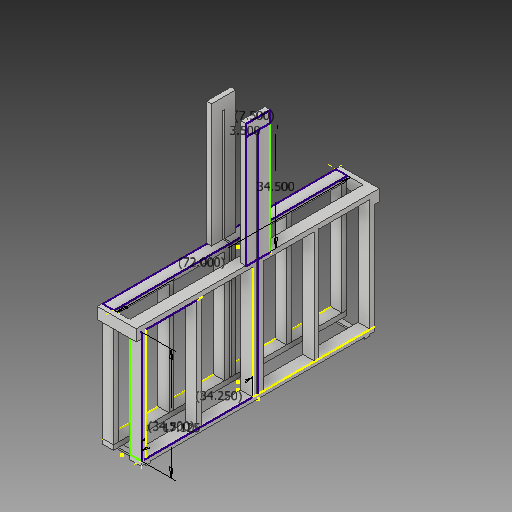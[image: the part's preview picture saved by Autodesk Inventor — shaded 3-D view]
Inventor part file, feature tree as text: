
AUTODESK INVENTOR PART (.ipt)
format: ipt  version: 2019 (Build 230136000, 136)  size: 366,080 bytes
history: native  units: in
note: dims shown in document units (in); Inventor stores cm internally (conversion verified against a paired STEP export)
features: sketch x19, extrude x8
ambient origin geometry x8: Origin, YZ Plane, XZ Plane, XY Plane, X Axis, Y Axis, Z Axis, Center Point
bodies: Solid1 (feature_tree), Solid2 (feature_tree)
feature tree (27):
  extrude  "Extrusion1"  Depth=72.0in
  extrude  "Extrusion3"  Depth=3.5in
  extrude  "Extrusion7"  Depth=1.5in
  extrude  "Extrusion8"  Depth=1.5in
  extrude  "Extrusion9"  Depth=1.5in
  extrude  "Extrusion11"  Depth=1.5in
  extrude  "Extrusion12"  Depth=1.5in
  extrude  "Extrusion13"  Depth=1.5in
  sketch  "Sketch19"  dims[d23=1.5in]
  sketch  "Sketch20"  dims[d24=3.5in]
  sketch  "Sketch21"  dims[d25=3.5in]
  sketch  "Sketch22"  dims[d26=3.5in]
  sketch  "Sketch23"  dims[d27=1.5in]
  sketch  "Sketch24"  dims[d28=1.5in]
  sketch  "Sketch25"  dims[d29=34.5in d30=0.0in]
  sketch  "Sketch26"  dims[d50=1.5in d51=0.0in]
  sketch  "Sketch27"  dims[d52=1.5in]
  sketch  "Sketch28"  dims[d53=3.5in]
  sketch  "Sketch29"  dims[d54=1.5in d55=3.5in d56=1.5in d57=3.5in d58=1.5in d59=3.5in d60=34.5in d61=0.0in d62=3.5in d63=0.0in d75=1.5in d76=1.5in d77=0.5in d78=0.0in d79=3.5in d80=1.5in d81=0.0in d82=1.5in d83=0.0in d84=34.5in d85=72.0in d87=34.5in d88=3.5in d89=7.5in d90=17.125in d91=34.25in]
  sketch  "Sketch1"  dims[d0=12.0in d1=72.0in]
  sketch  "Sketch2"  dims[d2=3.5in d3=3.5in]
  sketch  "Sketch10"  dims[d4=1.5in d5=0.0in d6=1.5in]
  sketch  "Sketch11"  dims[d8=0.5in d9=1.5in]
  sketch  "Sketch13"  dims[d10=1.5in d11=1.5in]
  sketch  "Sketch16"  dims[d17=1.5in d18=1.5in]
  sketch  "Sketch17"  dims[d19=3.5in d20=1.5in]
  sketch  "Sketch18"  dims[d21=3.5in d22=1.5in]
